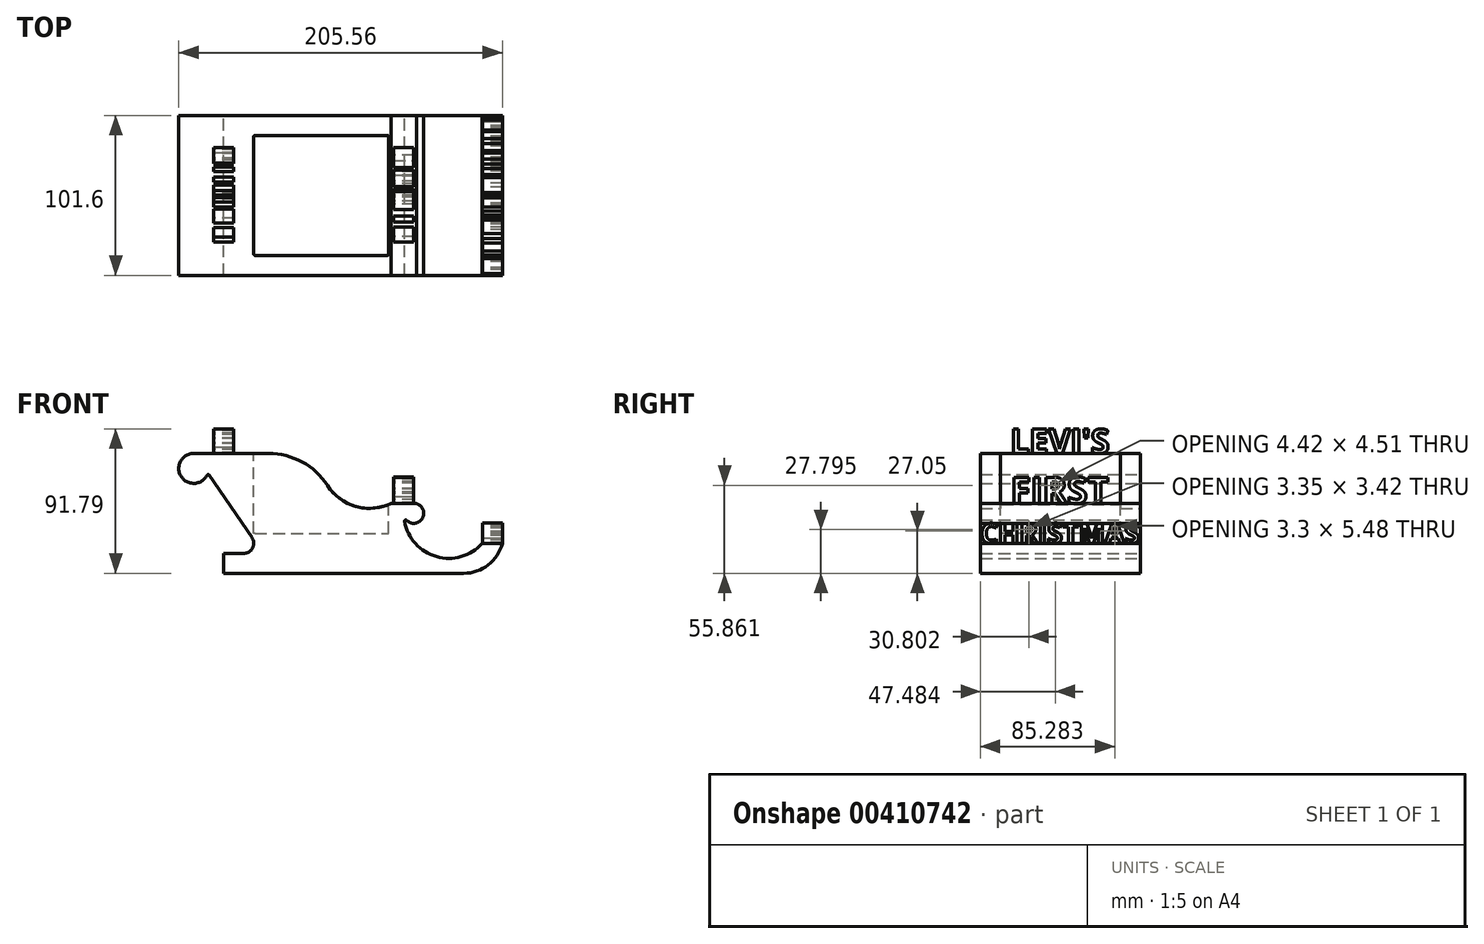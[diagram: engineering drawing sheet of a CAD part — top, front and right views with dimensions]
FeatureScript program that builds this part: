
annotation { "Feature Type Name" : "Feature", "Feature Type Description" : "" }
export const myFeature = defineFeature(function(context is Context, id is Id, definition is map)
    precondition{}
    {
        {
            var Q0;
            Q0=qCreatedBy(makeId("Front.planeOp"),FACE);
            var sketch = newSketch(context, id + "F0", { "sketchPlane" : qUnion([Q0])});
            skLineSegment(sketch, "E0", {"start": v(-152.4, 0) * mm, "end": v(0, 0) * mm});
            skArc(sketch, "E1", {"start": v(0, 0) * mm, "mid": v(15.55, 5.32) * mm, "end": v(24.6, 19.05) * mm});
            skArc(sketch, "E2", {"start": v(-37.63, 32.96) * mm, "mid": v(-17.27, 10.6) * mm, "end": v(11.77, 19.05) * mm});
            skLineSegment(sketch, "E3", {"start": v(11.77, 19.05) * mm, "end": v(24.6, 19.05) * mm});
            skArc(sketch, "E4", {"start": v(-36.29, 33.66) * mm, "mid": v(-26.73, 34.2) * mm, "end": v(-28.58, 43.6) * mm});
            skLineSegment(sketch, "E5", {"start": v(-38.1, 38.1) * mm, "end": v(-38.1, 38.1) * mm});
            skArc(sketch, "E6", {"start": v(-28.58, 43.6) * mm, "mid": v(-29.26, 43.98) * mm, "end": v(-29.96, 44.32) * mm});
            skArc(sketch, "E7", {"start": v(-86.5, 55.83) * mm, "mid": v(-68.54, 42.5) * mm, "end": v(-46.24, 44.32) * mm});
            skArc(sketch, "E8", {"start": v(-86.5, 55.83) * mm, "mid": v(-102.6, 70.78) * mm, "end": v(-123.87, 76.2) * mm});
            skLineSegment(sketch, "E9", {"start": v(-123.87, 76.2) * mm, "end": v(-171.45, 76.2) * mm});
            skArc(sketch, "E10", {"start": v(-171.45, 76.2) * mm, "mid": v(-179.6, 61.75) * mm, "end": v(-163.02, 62.24) * mm});
            skLineSegment(sketch, "E11", {"start": v(-161.66, 62.32) * mm, "end": v(-134.46, 22.64) * mm});
            skArc(sketch, "E12", {"start": v(-139.7, 12.7) * mm, "mid": v(-134.08, 16.09) * mm, "end": v(-134.46, 22.64) * mm});
            skLineSegment(sketch, "E13", {"start": v(-139.7, 12.7) * mm, "end": v(-152.4, 12.7) * mm});
            skLineSegment(sketch, "E14", {"start": v(-152.4, 12.7) * mm, "end": v(-152.4, 0) * mm});
            skPoint(sketch, "E15.visualSharp", {"position": v(-38.1, 38.1) * mm});
            skArc(sketch, "E15.filletArc", {"start": v(-36.29, 33.66) * mm, "mid": v(-37.22, 33.8) * mm, "end": v(-37.63, 32.96) * mm});
            skPoint(sketch, "E16.visualSharp", {"position": v(-162.47, 63.5) * mm});
            skArc(sketch, "E16.filletArc", {"start": v(-161.66, 62.32) * mm, "mid": v(-162.36, 62.67) * mm, "end": v(-163.02, 62.24) * mm});
            skLineSegment(sketch, "E17", {"start": v(-46.24, 44.32) * mm, "end": v(-29.96, 44.32) * mm});
            skSolve(sketch);
        }
        {
            var Q0;
            Q0=makeQuery(id+"F0.imprint","IMPRINT",FACE,{"disambiguationData":[TD([[makeQuery(id+"F0.imprint","IMPRINT",EDGE,{"derivedFrom":sQuery(id+"F0.wireOp",EDGE,"E0")}),1.0]])]});
            extrude(context, id + "F1", {"entities" : qUnion([Q0]), "endBound" : BoundingType.SYMMETRIC, "depth" : 101.6 * mm});
        }
        {
            var Q0;
            Q0=makeQuery(id+"F1.opExtrude","SWEPT_FACE",FACE,{"disambiguationData":[OSD([sQuery(id+"F0.wireOp",EDGE,"E9")])]});
            var sketch = newSketch(context, id + "F2", { "sketchPlane" : qUnion([Q0])});
            skLineSegment(sketch, "E18.0", {"start": v(-123.87, 50.8) * mm, "end": v(-171.45, 50.8) * mm});
            skLineSegment(sketch, "E19.0", {"start": v(-86.5, 50.8) * mm, "end": v(-123.87, 50.8) * mm});
            skLineSegment(sketch, "E20.0", {"start": v(-86.5, 50.8) * mm, "end": v(-46.24, 50.8) * mm});
            skLineSegment(sketch, "E21.0", {"start": v(-28.58, 50.8) * mm, "end": v(-46.24, 50.8) * mm});
            skLineSegment(sketch, "E22.0", {"start": v(-28.58, -50.8) * mm, "end": v(-28.58, -50.8) * mm});
            skLineSegment(sketch, "E23.0", {"start": v(-86.5, -50.8) * mm, "end": v(-28.58, -50.8) * mm});
            skLineSegment(sketch, "E24.0", {"start": v(-86.5, -50.8) * mm, "end": v(-123.87, -50.8) * mm});
            skLineSegment(sketch, "E25.0", {"start": v(-123.87, -50.8) * mm, "end": v(-171.45, -50.8) * mm});
            skLineSegment(sketch, "E26.0", {"start": v(-171.45, -50.8) * mm, "end": v(-171.45, 50.8) * mm});
            skLineSegment(sketch, "E27.0", {"start": v(-28.58, -50.8) * mm, "end": v(-28.58, 50.8) * mm});
            skLineSegment(sketch, "E28.bottom", {"start": v(-132.56, 38.1) * mm, "end": v(-48.42, 38.1) * mm});
            skLineSegment(sketch, "E28.top", {"start": v(-132.56, -38.1) * mm, "end": v(-48.42, -38.1) * mm});
            skLineSegment(sketch, "E28.left", {"start": v(-133.35, 37.3) * mm, "end": v(-133.35, -37.3) * mm});
            skLineSegment(sketch, "E28.right", {"start": v(-47.63, 37.3) * mm, "end": v(-47.62, -37.3) * mm});
            skPoint(sketch, "E29.visualSharp", {"position": v(-133.35, 38.1) * mm});
            skArc(sketch, "E29.filletArc", {"start": v(-132.56, 38.1) * mm, "mid": v(-133.12, 37.87) * mm, "end": v(-133.35, 37.3) * mm});
            skPoint(sketch, "E30.visualSharp", {"position": v(-133.35, -38.1) * mm});
            skArc(sketch, "E30.filletArc", {"start": v(-133.35, -37.3) * mm, "mid": v(-133.12, -37.87) * mm, "end": v(-132.56, -38.1) * mm});
            skPoint(sketch, "E31.visualSharp", {"position": v(-47.62, -38.1) * mm});
            skArc(sketch, "E31.filletArc", {"start": v(-48.42, -38.1) * mm, "mid": v(-47.86, -37.87) * mm, "end": v(-47.62, -37.3) * mm});
            skPoint(sketch, "E32.visualSharp", {"position": v(-47.63, 38.1) * mm});
            skArc(sketch, "E32.filletArc", {"start": v(-47.62, 37.3) * mm, "mid": v(-47.86, 37.87) * mm, "end": v(-48.42, 38.1) * mm});
            skSolve(sketch);
        }
        {
            var Q0;
            Q0=makeQuery(id+"F2.imprint","IMPRINT",FACE,{"disambiguationData":[TD([[makeQuery(id+"F2.imprint","IMPRINT",EDGE,{"derivedFrom":sQuery(id+"F2.wireOp",EDGE,"E28.left")}),1.0]])]});
            var Q1;
            Q1=makeQuery(id+"F2.imprint","IMPRINT",FACE,{"disambiguationData":[TD([[makeQuery(id+"F2.imprint","IMPRINT",EDGE,{"derivedFrom":sQuery(id+"F2.wireOp",EDGE,"E28.right")}),-1.0]])]});
            extrude(context, id + "F3", {"entities" : qUnion([Q0, Q1]), "operationType" : NewBodyOperationType.REMOVE, "oppositeDirection" : true, "depth" : 50.8 * mm});
        }
        {
            var Q0;
            Q0=makeQuery(id+"F3.boolean.opBoolean","COPY",FACE,{"derivedFrom":makeQuery(id+"F3.opExtrude","SWEPT_FACE",FACE,{"disambiguationData":[OSD([sQuery(id+"F2.wireOp",EDGE,"E28.left")])]})});
            cPlane(context, id + "F4", {"entities" : qUnion([Q0]), "cplaneType" : CPlaneType.OFFSET, "offset" : 19.05 * mm, "oppositeDirection" : true, "width" : 152.4 * mm, "height" : 152.4 * mm});
        }
        {
            var Q0;
            Q0=qCreatedBy(id+"F4.planeOp",FACE);
            var sketch = newSketch(context, id + "F5", { "sketchPlane" : qUnion([Q0])});
            skLineSegment(sketch, "E33.0", {"start": v(37.3, 76.2) * mm, "end": v(-37.3, 76.2) * mm});
            skText(sketch, "E34", { "text": "LEVI\'S", "fontName": "OpenSans-Bold.ttf"});
            const initialGuessF5  = {"E34": [-0.03175, 0.0762, 1, 0, 0.0155]};
            skSetInitialGuess(sketch, initialGuessF5);
            skSolve(sketch);
        }
        {
            var Q0;
            Q0 = qSketchRegion(id + "F5", true);
            extrude(context, id + "F6", {"entities" : qUnion([Q0]), "operationType" : NewBodyOperationType.ADD, "endBound" : BoundingType.SYMMETRIC, "depth" : 12.7 * mm});
        }
        {
            var Q0;
            Q0=makeQuery(id+"F1.opExtrude","CAP_EDGE",EDGE,{"disambiguationData":[OSD([sQuery(id+"F0.wireOp",EDGE,"E17")])],"isStart":false});
            cPoint(context, id + "F7", {"entities" : qUnion([Q0]), "parameter" : 0.5});
        }
        {
            var Q0;
            Q0 = qCreatedBy(id + "F7" ,VERTEX);
            var Q1;
            Q1=makeQuery(id+"F1.opExtrude","CAP_EDGE",EDGE,{"disambiguationData":[OSD([sQuery(id+"F0.wireOp",EDGE,"E17")])],"isStart":false});
            cPlane(context, id + "F8", {"entities" : qUnion([Q0, Q1]), "cplaneType" : CPlaneType.LINE_POINT, "offset" : 25.4 * mm, "width" : 152.4 * mm, "height" : 152.4 * mm});
        }
        {
            var Q0;
            Q0=qCreatedBy(id+"F8.planeOp",FACE);
            var sketch = newSketch(context, id + "F9", { "sketchPlane" : qUnion([Q0])});
            skLineSegment(sketch, "E35.0", {"start": v(-50.8, 44.32) * mm, "end": v(50.8, 44.32) * mm, "construction": true});
            skText(sketch, "E36", { "text": "FIRST", "fontName": "OpenSans-Bold.ttf"});
            const initialGuessF9  = {"E36": [-0.03175, 0.04432, 1, 0, 0.01684]};
            skSetInitialGuess(sketch, initialGuessF9);
            skSolve(sketch);
        }
        {
            var Q0;
            Q0 = qSketchRegion(id + "F9", true);
            extrude(context, id + "F10", {"entities" : qUnion([Q0]), "operationType" : NewBodyOperationType.ADD, "endBound" : BoundingType.SYMMETRIC, "depth" : 12.7 * mm});
        }
        {
            var Q0;
            Q0=makeQuery(id+"F1.opExtrude","CAP_EDGE",EDGE,{"disambiguationData":[OSD([sQuery(id+"F0.wireOp",EDGE,"E3")])],"isStart":false});
            cPoint(context, id + "F11", {"entities" : qUnion([Q0]), "parameter" : 0.5});
        }
        {
            var Q0;
            Q0 = qCreatedBy(id + "F11" ,VERTEX);
            var Q1;
            Q1=makeQuery(id+"F1.opExtrude","CAP_EDGE",EDGE,{"disambiguationData":[OSD([sQuery(id+"F0.wireOp",EDGE,"E3")])],"isStart":false});
            cPlane(context, id + "F12", {"entities" : qUnion([Q0, Q1]), "cplaneType" : CPlaneType.LINE_POINT, "offset" : 25.4 * mm, "width" : 152.4 * mm, "height" : 152.4 * mm});
        }
        {
            var Q0;
            Q0=qCreatedBy(id+"F12.planeOp",FACE);
            var sketch = newSketch(context, id + "F13", { "sketchPlane" : qUnion([Q0])});
            skText(sketch, "E37", { "text": "CHRISTMAS", "fontName": "OpenSans-Bold.ttf"});
            skLineSegment(sketch, "E38.0", {"start": v(-50.8, 19.05) * mm, "end": v(50.8, 19.05) * mm, "construction": true});
            const initialGuessF13  = {"E37": [-0.0508, 0.01905, 1, 0, 0.01276]};
            skSetInitialGuess(sketch, initialGuessF13);
            skSolve(sketch);
        }
        {
            var Q0;
            Q0 = qSketchRegion(id + "F13", true);
            extrude(context, id + "F14", {"entities" : qUnion([Q0]), "operationType" : NewBodyOperationType.ADD, "endBound" : BoundingType.SYMMETRIC, "depth" : 12.7 * mm});
        }
    });
